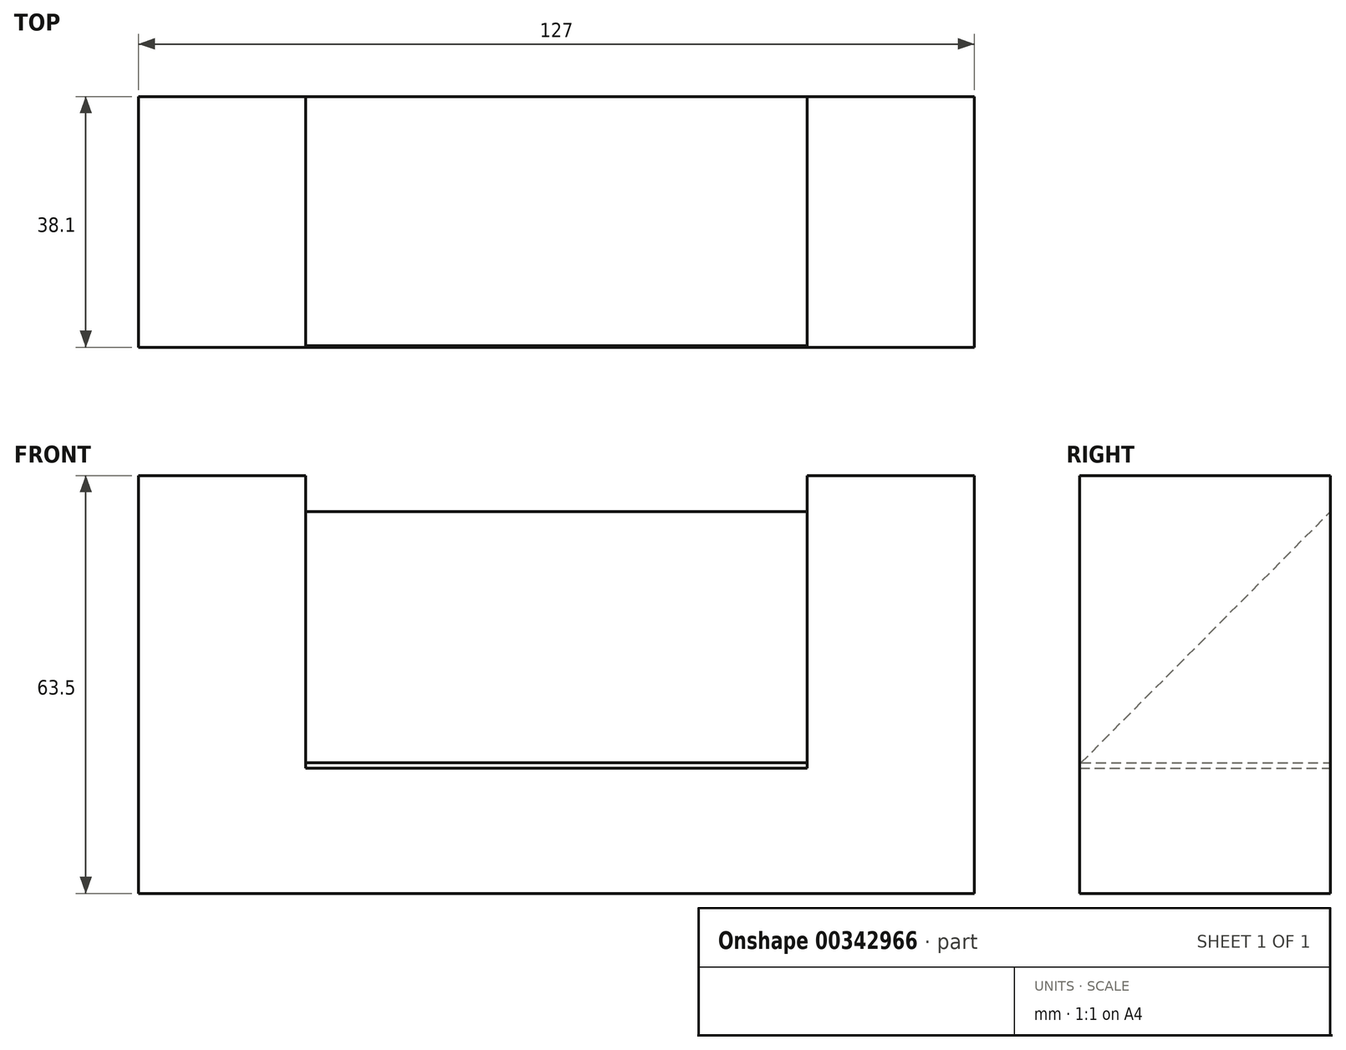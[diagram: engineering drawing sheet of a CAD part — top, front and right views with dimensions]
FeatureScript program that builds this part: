
annotation { "Feature Type Name" : "Feature", "Feature Type Description" : "" }
export const myFeature = defineFeature(function(context is Context, id is Id, definition is map)
    precondition{}
    {
        {
            var Q0;
            Q0=qCreatedBy(makeId("Front.planeOp"),FACE);
            var sketch = newSketch(context, id + "F0", { "sketchPlane" : qUnion([Q0])});
            skLineSegment(sketch, "E0", {"start": v(-41.56, 31.87) * mm, "end": v(-16.16, 31.87) * mm});
            skLineSegment(sketch, "E1", {"start": v(-41.56, 31.87) * mm, "end": v(-41.56, -31.63) * mm});
            skLineSegment(sketch, "E2", {"start": v(-41.56, -31.63) * mm, "end": v(85.44, -31.63) * mm});
            skLineSegment(sketch, "E3", {"start": v(85.44, -31.63) * mm, "end": v(85.44, 31.87) * mm});
            skLineSegment(sketch, "E4", {"start": v(85.44, 31.87) * mm, "end": v(60.04, 31.87) * mm});
            skLineSegment(sketch, "E5", {"start": v(-16.16, 31.87) * mm, "end": v(-16.16, -12.58) * mm});
            skLineSegment(sketch, "E6", {"start": v(60.04, 31.87) * mm, "end": v(60.04, -12.58) * mm});
            skLineSegment(sketch, "E7", {"start": v(-16.16, -12.58) * mm, "end": v(60.04, -12.58) * mm});
            skSolve(sketch);
        }
        {
            var Q0;
            Q0 = qSketchRegion(id + "F0", true);
            extrude(context, id + "F1", {"entities" : qUnion([Q0]), "depth" : 38.1 * mm});
        }
        {
            var Q0;
            Q0=qCreatedBy(makeId("Right.planeOp"),FACE);
            var sketch = newSketch(context, id + "F2", { "sketchPlane" : qUnion([Q0])});
            skLineSegment(sketch, "E8", {"start": v(0, -11.8) * mm, "end": v(-37.9, -11.8) * mm});
            skLineSegment(sketch, "E9", {"start": v(0, -11.8) * mm, "end": v(0, 26.38) * mm});
            skLineSegment(sketch, "E10", {"start": v(0, 26.38) * mm, "end": v(-37.9, -11.8) * mm});
            skSolve(sketch);
        }
        {
            var Q0;
            Q0 = qSketchRegion(id + "F2", true);
            extrude(context, id + "F3", {"entities" : qUnion([Q0]), "operationType" : NewBodyOperationType.ADD, "depth" : 76.2 * mm, "hasSecondDirection" : true, "secondDirectionOppositeDirection" : true, "secondDirectionDepth" : 25.4 * mm});
        }
    });
